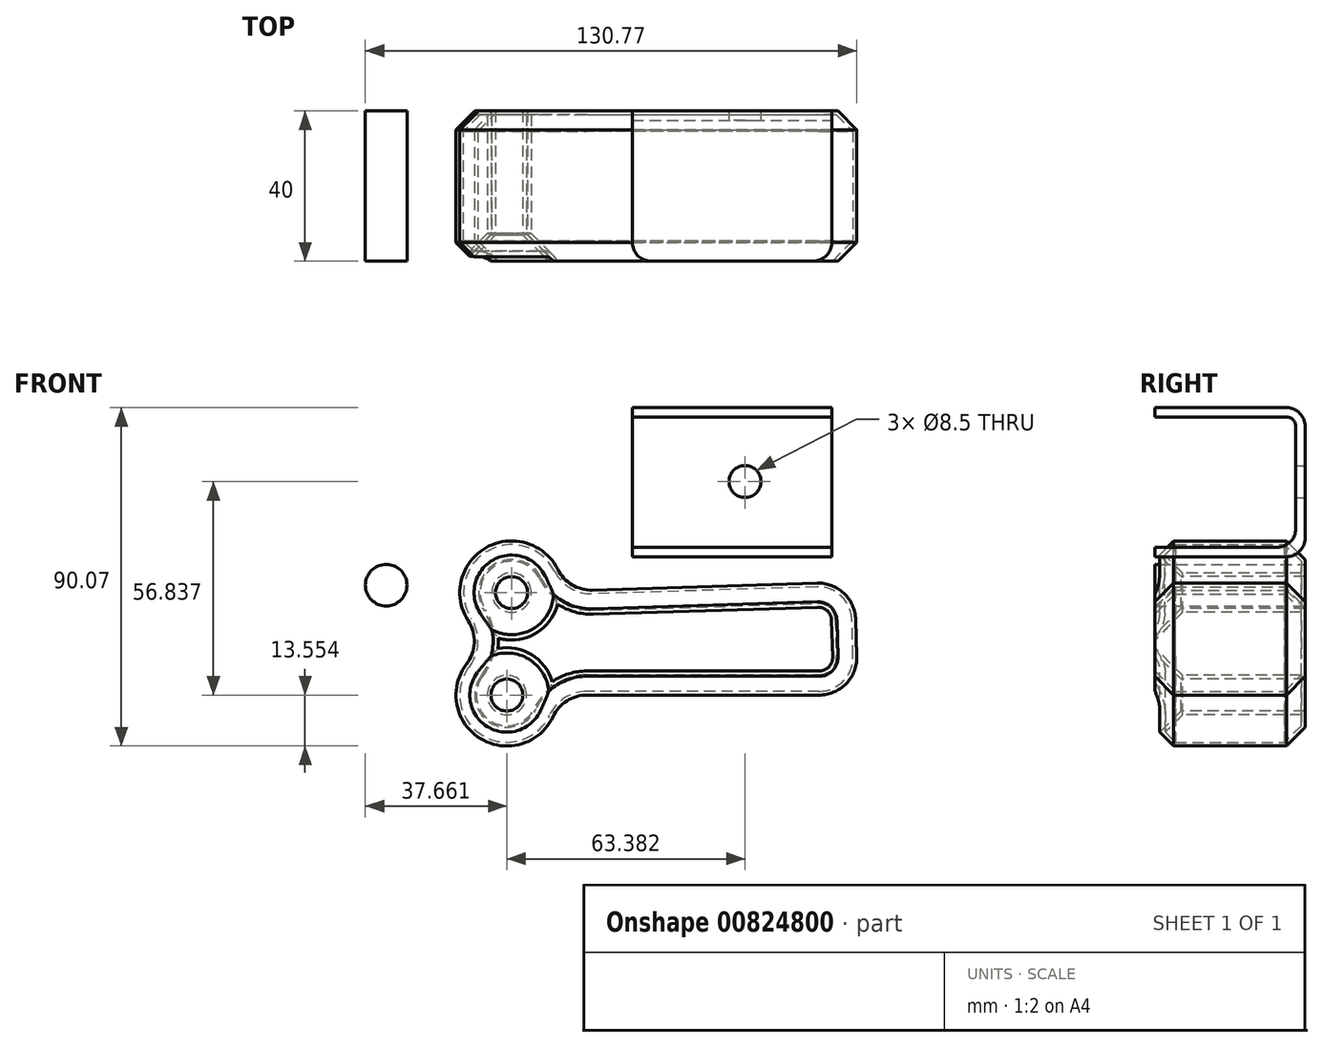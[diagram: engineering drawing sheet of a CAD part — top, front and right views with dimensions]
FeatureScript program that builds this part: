
annotation { "Feature Type Name" : "Feature", "Feature Type Description" : "" }
export const myFeature = defineFeature(function(context is Context, id is Id, definition is map)
    precondition{}
    {
        {
            var Q0;
            Q0=qCreatedBy(makeId("Front.planeOp"),FACE);
            var sketch = newSketch(context, id + "F0", { "sketchPlane" : qUnion([Q0])});
            skLineSegment(sketch, "E0", {"start": v(-66.16, 48.15) * mm, "end": v(25.14, 50.98) * mm});
            skLineSegment(sketch, "E1", {"start": v(-67.4, 20.86) * mm, "end": v(26, 20.86) * mm});
            skLineSegment(sketch, "E2", {"start": v(25.14, 50.98) * mm, "end": v(26, 20.86) * mm});
            skCircle(sketch, "E3", {"center": v(-99.52, 50.12) * mm, "radius": 5.54 * mm});
            skCircle(sketch, "E4", {"center": v(-66.16, 48.15) * mm, "radius": 13.76 * mm});
            skCircle(sketch, "E5", {"center": v(-67.4, 20.86) * mm, "radius": 13.55 * mm});
            skLineSegment(sketch, "E6.bottom", {"start": v(-34.02, 97.38) * mm, "end": v(19.1, 97.38) * mm});
            skLineSegment(sketch, "E6.top", {"start": v(-34.02, 57.7) * mm, "end": v(19.1, 57.7) * mm});
            skLineSegment(sketch, "E6.left", {"start": v(-34.02, 97.38) * mm, "end": v(-34.02, 57.7) * mm});
            skLineSegment(sketch, "E6.right", {"start": v(19.1, 97.38) * mm, "end": v(19.1, 57.7) * mm});
            skSolve(sketch);
        }
        {
            var Q0;
            Q0=makeQuery(id+"F0.imprint","IMPRINT",FACE,{"disambiguationData":[TD([[makeQuery(id+"F0.imprint","IMPRINT",EDGE,{"derivedFrom":sQuery(id+"F0.wireOp",EDGE,"E6.bottom")}),-1.0]])]});
            var Q1;
            {var subQ0=sQuery(id+"F0.wireOp",EDGE,"E4");var subQ1=makeQuery(id+"F0.imprint","INTERSECT",VERTEX,{"derivedFrom":[sQuery(id+"F0.wireOp",EDGE,"E0"),subQ0]});Q1=makeQuery(id+"F0.imprint","IMPRINT",FACE,{"disambiguationData":[TD([[makeQuery(id+"F0.imprint","IMPRINT",EDGE,{"disambiguationData":[TD([[subQ1,-1.0]])],"derivedFrom":subQ0}),1.0]])]});}
            var Q2;
            {var subQ0=sQuery(id+"F0.wireOp",EDGE,"E5");var subQ1=makeQuery(id+"F0.imprint","INTERSECT",VERTEX,{"derivedFrom":[sQuery(id+"F0.wireOp",EDGE,"E1"),subQ0]});Q2=makeQuery(id+"F0.imprint","IMPRINT",FACE,{"disambiguationData":[TD([[makeQuery(id+"F0.imprint","IMPRINT",EDGE,{"disambiguationData":[TD([[subQ1,-1.0]])],"derivedFrom":subQ0}),1.0]])]});}
            var Q3;
            {var subQ0=sQuery(id+"F0.wireOp",EDGE,"E2");Q3=makeQuery(id+"F0.imprint","IMPRINT",FACE,{"disambiguationData":[TD([[makeQuery(id+"F0.imprint","IMPRINT",EDGE,{"derivedFrom":subQ0}),-1.0]])]});}
            var Q4;
            Q4=makeQuery(id+"F0.imprint","IMPRINT",FACE,{"disambiguationData":[TD([[makeQuery(id+"F0.imprint","IMPRINT",EDGE,{"derivedFrom":sQuery(id+"F0.wireOp",EDGE,"E3")}),1.0]])]});
            extrude(context, id + "F1", {"entities" : qUnion([Q0, Q1, Q2, Q3, Q4]), "depth" : 40 * mm, "offsetDistance" : 25 * mm});
        }
        {
            var Q0;
            Q0=makeQuery(id+"F1.opExtrude","CAP_FACE",FACE,{"disambiguationData":[OSD([sQuery(id+"F0.wireOp",EDGE,"E0"),sQuery(id+"F0.wireOp",EDGE,"E1"),sQuery(id+"F0.wireOp",EDGE,"E2"),sQuery(id+"F0.wireOp",EDGE,"E4"),sQuery(id+"F0.wireOp",EDGE,"E5")])],"isStart":false});
            var sketch = newSketch(context, id + "F2", { "sketchPlane" : qUnion([Q0])});
            skPoint(sketch, "E7", {"position": v(-66.16, 48.15) * mm});
            skPoint(sketch, "E8", {"position": v(-67.4, 20.86) * mm});
            skSolve(sketch);
        }
        {
            var Q0;
            Q0=sQuery(id+"F2.wireOp",VERTEX,"E7");
            var Q1;
            Q1=sQuery(id+"F2.wireOp",VERTEX,"E8");
            var Q2;
            Q2=makeQuery(id+"F1.opExtrude","SWEPT_BODY",BODY,{"disambiguationData":[OSD([sQuery(id+"F0.wireOp",EDGE,"E0"),sQuery(id+"F0.wireOp",EDGE,"E1"),sQuery(id+"F0.wireOp",EDGE,"E2"),sQuery(id+"F0.wireOp",EDGE,"E4"),sQuery(id+"F0.wireOp",EDGE,"E5")])]});
            hole(context, id + "F3", {"style" : HoleStyle.C_SINK, "endStyle" : HoleEndStyle.THROUGH, "standardTappedOrClearance" : lookupTablePath({ "standard" : "ISO", "engagement" : "75%", "pitch" : "1.5 mm", "size" : "M10", "type" : "Tapped" }), "standardBlindInLast" : lookupTablePath({ "standard" : "ISO", "engagement" : "75%", "pitch" : "1.5 mm", "size" : "M10", "type" : "Tapped" }), "holeDiameter" : 8.5 * mm, "cSinkDiameter" : 22.4 * mm, "cSinkAngle" : 90 * degree, "majorDiameter" : 10 * mm, "showTappedDepth" : true, "isTappedThrough" : true, "tappedDepth" : 12 * mm, "tapClearance" : 3, "locations" : qUnion([Q0, Q1]), "scope" : qUnion([Q2])});
        }
        {
            var Q0;
            Q0=makeQuery(id+"F1.opExtrude","SWEPT_EDGE",EDGE,{"disambiguationData":[OSD([sQuery(id+"F0.wireOp",EDGE,"E4"),sQuery(id+"F0.wireOp",EDGE,"E5")])]});
            var Q1;
            Q1=makeQuery(id+"F1.opExtrude","SWEPT_EDGE",EDGE,{"disambiguationData":[OSD([sQuery(id+"F0.wireOp",EDGE,"E0"),sQuery(id+"F0.wireOp",EDGE,"E4")])]});
            var Q2;
            Q2=makeQuery(id+"F1.opExtrude","SWEPT_EDGE",EDGE,{"disambiguationData":[OSD([sQuery(id+"F0.wireOp",EDGE,"E1"),sQuery(id+"F0.wireOp",EDGE,"E5")])]});
            var Q3;
            Q3=makeQuery(id+"F1.opExtrude","SWEPT_EDGE",EDGE,{"disambiguationData":[OSD([sQuery(id+"F0.wireOp",EDGE,"E0"),sQuery(id+"F0.wireOp",EDGE,"E2")])]});
            var Q4;
            Q4=makeQuery(id+"F1.opExtrude","SWEPT_EDGE",EDGE,{"disambiguationData":[OSD([sQuery(id+"F0.wireOp",EDGE,"E1"),sQuery(id+"F0.wireOp",EDGE,"E2")])]});
            fillet(context, id + "F4", {"entities" : qUnion([Q0, Q1, Q2, Q3, Q4]), "radius" : 10 * mm, "tangentPropagation" : true, "allowEdgeOverflow" : false});
        }
        {
            var Q0;
            Q0=makeQuery(id+"F1.opExtrude","CAP_EDGE",EDGE,{"disambiguationData":[OSD([sQuery(id+"F0.wireOp",EDGE,"E0")])],"isStart":false});
            var Q1;
            Q1=makeQuery(id+"F1.opExtrude","CAP_EDGE",EDGE,{"disambiguationData":[OSD([sQuery(id+"F0.wireOp",EDGE,"E0")])],"isStart":true});
            chamfer(context, id + "F5", {"entities" : qUnion([Q0, Q1]), "width" : 5 * mm, "tangentPropagation" : true});
        }
        {
            var Q0;
            Q0=makeQuery(id+"F1.opExtrude","CAP_FACE",FACE,{"disambiguationData":[OSD([sQuery(id+"F0.wireOp",EDGE,"E0"),sQuery(id+"F0.wireOp",EDGE,"E1"),sQuery(id+"F0.wireOp",EDGE,"E2"),sQuery(id+"F0.wireOp",EDGE,"E4"),sQuery(id+"F0.wireOp",EDGE,"E5")])],"isStart":false});
            shell(context, id + "F6", {"entities" : qUnion([Q0]), "thickness" : 1 * mm});
        }
        {
            var Q0;
            Q0=makeQuery(id+"F1.opExtrude","CAP_FACE",FACE,{"disambiguationData":[OSD([sQuery(id+"F0.wireOp",EDGE,"E6.bottom"),sQuery(id+"F0.wireOp",EDGE,"E6.top"),sQuery(id+"F0.wireOp",EDGE,"E6.left"),sQuery(id+"F0.wireOp",EDGE,"E6.right")])],"isStart":false});
            var Q1;
            Q1=makeQuery(id+"F1.opExtrude","SWEPT_FACE",FACE,{"disambiguationData":[OSD([sQuery(id+"F0.wireOp",EDGE,"E6.left")])]});
            var Q2;
            Q2=makeQuery(id+"F1.opExtrude","SWEPT_FACE",FACE,{"disambiguationData":[OSD([sQuery(id+"F0.wireOp",EDGE,"E6.right")])]});
            shell(context, id + "F7", {"entities" : qUnion([Q0, Q1, Q2]), "thickness" : 2.5 * mm});
        }
        {
            var Q0;
            Q0=makeQuery(id+"F1.opExtrude","CAP_EDGE",EDGE,{"disambiguationData":[OSD([sQuery(id+"F0.wireOp",EDGE,"E6.bottom")])],"isStart":true});
            var Q1;
            {var subQ0=sQuery(id+"F0.wireOp",EDGE,"E6.top");Q1=makeQuery(id+"F7.opShell","OFFSET_EDGE",EDGE,{"disambiguationData":[OSD([subQ0]),TDD([makeQuery(id+"F1.opExtrude","CAP_EDGE",EDGE,{"disambiguationData":[OSD([subQ0])],"isStart":true})])]});}
            var Q2;
            Q2=makeQuery(id+"F1.opExtrude","CAP_EDGE",EDGE,{"disambiguationData":[OSD([sQuery(id+"F0.wireOp",EDGE,"E6.top")])],"isStart":true});
            var Q3;
            Q3=makeQuery(id+"F1.opExtrude","CAP_EDGE",EDGE,{"disambiguationData":[OSD([sQuery(id+"F0.wireOp",EDGE,"E6.right")])],"isStart":false});
            var Q4;
            {var subQ0=sQuery(id+"F0.wireOp",EDGE,"E6.right");Q4=makeQuery(id+"F7.opShell","OFFSET_EDGE",EDGE,{"disambiguationData":[OSD([subQ0]),TDD([makeQuery(id+"F1.opExtrude","CAP_EDGE",EDGE,{"disambiguationData":[OSD([subQ0])],"isStart":false})])]});}
            var Q5;
            Q5=makeQuery(id+"F1.opExtrude","CAP_EDGE",EDGE,{"disambiguationData":[OSD([sQuery(id+"F0.wireOp",EDGE,"E6.left")])],"isStart":false});
            var Q6;
            {var subQ0=sQuery(id+"F0.wireOp",EDGE,"E6.left");Q6=makeQuery(id+"F7.opShell","OFFSET_EDGE",EDGE,{"disambiguationData":[OSD([subQ0]),TDD([makeQuery(id+"F1.opExtrude","CAP_EDGE",EDGE,{"disambiguationData":[OSD([subQ0])],"isStart":false})])]});}
            fillet(context, id + "F8", {"entities" : qUnion([Q0, Q1, Q2, Q3, Q4, Q5, Q6]), "radius" : 5 * mm, "tangentPropagation" : true, "allowEdgeOverflow" : false});
        }
        {
            var Q0;
            {var subQ0=sQuery(id+"F0.wireOp",EDGE,"E6.bottom");Q0=makeQuery(id+"F7.opShell","OFFSET_EDGE",EDGE,{"disambiguationData":[OSD([subQ0]),TDD([makeQuery(id+"F1.opExtrude","CAP_EDGE",EDGE,{"disambiguationData":[OSD([subQ0])],"isStart":true})])]});}
            fillet(context, id + "F9", {"entities" : qUnion([Q0]), "radius" : 2.5 * mm, "tangentPropagation" : true, "allowEdgeOverflow" : false});
        }
        {
            var Q0;
            Q0=makeQuery(id+"F1.opExtrude","CAP_FACE",FACE,{"disambiguationData":[OSD([sQuery(id+"F0.wireOp",EDGE,"E6.bottom"),sQuery(id+"F0.wireOp",EDGE,"E6.top"),sQuery(id+"F0.wireOp",EDGE,"E6.left"),sQuery(id+"F0.wireOp",EDGE,"E6.right")])],"isStart":true});
            var sketch = newSketch(context, id + "F10", { "sketchPlane" : qUnion([Q0])});
            skPoint(sketch, "E9", {"position": v(4.02, 77.7) * mm});
            skSolve(sketch);
        }
        {
            var Q0;
            Q0=sQuery(id+"F10.wireOp",VERTEX,"E9");
            var Q1;
            Q1=makeQuery(id+"F1.opExtrude","SWEPT_BODY",BODY,{"disambiguationData":[OSD([sQuery(id+"F0.wireOp",EDGE,"E6.bottom"),sQuery(id+"F0.wireOp",EDGE,"E6.top"),sQuery(id+"F0.wireOp",EDGE,"E6.left"),sQuery(id+"F0.wireOp",EDGE,"E6.right")])]});
            hole(context, id + "F11", {"style" : HoleStyle.SIMPLE, "endStyle" : HoleEndStyle.THROUGH, "holeDiameter" : 8.5 * mm, "majorDiameter" : 10 * mm, "isTappedThrough" : true, "tappedDepth" : 12 * mm, "tapClearance" : 3, "locations" : qUnion([Q0]), "scope" : qUnion([Q1])});
        }
    });
